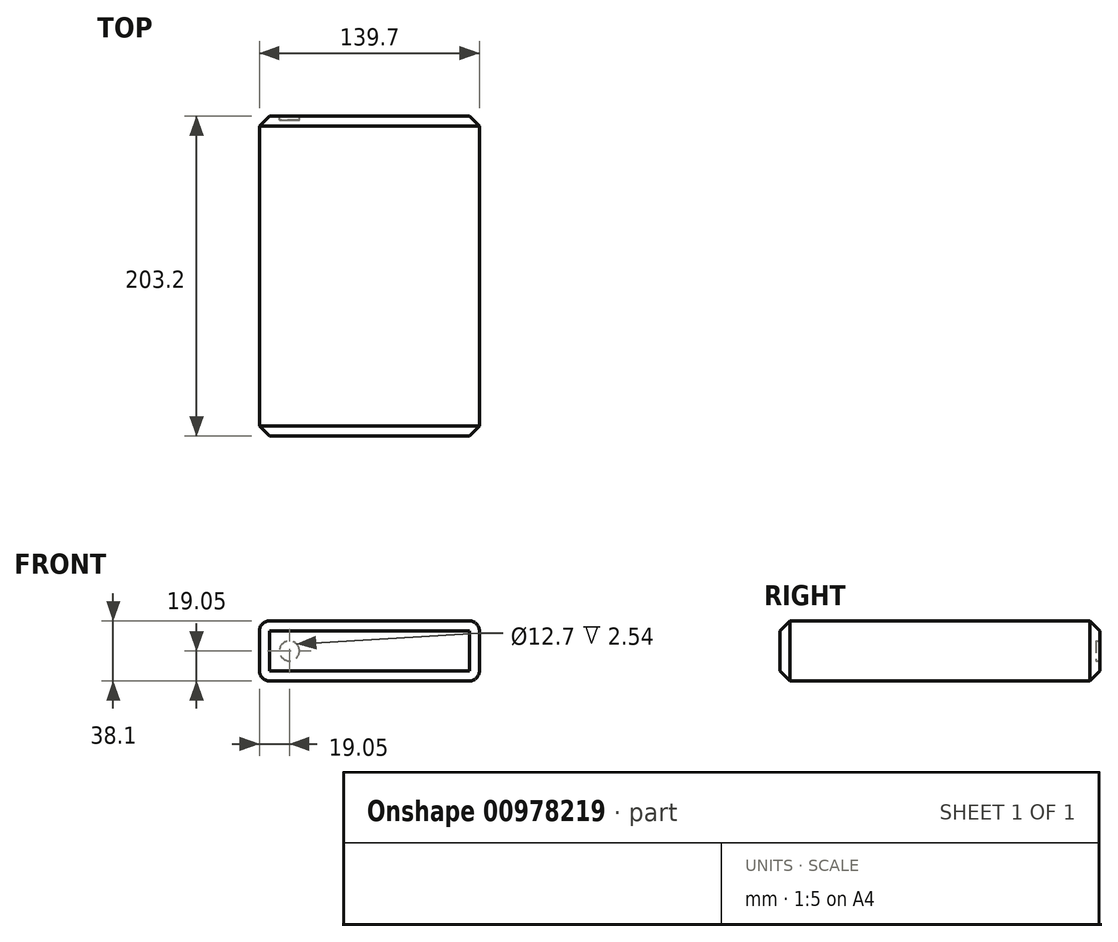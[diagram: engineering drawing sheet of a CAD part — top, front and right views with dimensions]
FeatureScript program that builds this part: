
annotation { "Feature Type Name" : "Feature", "Feature Type Description" : "" }
export const myFeature = defineFeature(function(context is Context, id is Id, definition is map)
    precondition{}
    {
        {
            var Q0;
            Q0=qCreatedBy(makeId("Front.planeOp"),FACE);
            var sketch = newSketch(context, id + "F0", { "sketchPlane" : qUnion([Q0])});
            skLineSegment(sketch, "E0.bottom", {"start": v(-69.85, 19.05) * mm, "end": v(69.85, 19.05) * mm});
            skLineSegment(sketch, "E0.top", {"start": v(-69.85, -19.05) * mm, "end": v(69.85, -19.05) * mm});
            skLineSegment(sketch, "E0.left", {"start": v(-69.85, 19.05) * mm, "end": v(-69.85, -19.05) * mm});
            skLineSegment(sketch, "E0.right", {"start": v(69.85, 19.05) * mm, "end": v(69.85, -19.05) * mm});
            skLineSegment(sketch, "E1", {"start": v(0, 0) * mm, "end": v(0, 19.05) * mm, "construction": true});
            skLineSegment(sketch, "E2", {"start": v(0, 0) * mm, "end": v(69.85, 0) * mm, "construction": true});
            skSolve(sketch);
        }
        {
            var Q0;
            Q0=makeQuery(id+"F0.imprint","IMPRINT",FACE,{"disambiguationData":[TD([[makeQuery(id+"F0.imprint","IMPRINT",EDGE,{"derivedFrom":sQuery(id+"F0.wireOp",EDGE,"E0.bottom")}),-1.0]])]});
            extrude(context, id + "F1", {"entities" : qUnion([Q0]), "depth" : 203.2 * mm, "offsetDistance" : 25.4 * mm});
        }
        {
            var Q0;
            Q0=makeQuery(id+"F1.opExtrude","SWEPT_EDGE",EDGE,{"disambiguationData":[OSD([sQuery(id+"F0.wireOp",EDGE,"E0.bottom"),sQuery(id+"F0.wireOp",EDGE,"E0.left")])]});
            var Q1;
            Q1=makeQuery(id+"F1.opExtrude","SWEPT_EDGE",EDGE,{"disambiguationData":[OSD([sQuery(id+"F0.wireOp",EDGE,"E0.top"),sQuery(id+"F0.wireOp",EDGE,"E0.left")])]});
            var Q2;
            Q2=makeQuery(id+"F1.opExtrude","SWEPT_EDGE",EDGE,{"disambiguationData":[OSD([sQuery(id+"F0.wireOp",EDGE,"E0.bottom"),sQuery(id+"F0.wireOp",EDGE,"E0.right")])]});
            var Q3;
            Q3=makeQuery(id+"F1.opExtrude","SWEPT_EDGE",EDGE,{"disambiguationData":[OSD([sQuery(id+"F0.wireOp",EDGE,"E0.top"),sQuery(id+"F0.wireOp",EDGE,"E0.right")])]});
            fillet(context, id + "F2", {"entities" : qUnion([Q0, Q1, Q2, Q3]), "radius" : 6.35 * mm, "tangentPropagation" : true, "allowEdgeOverflow" : false});
        }
        {
            var Q0;
            Q0=makeQuery(id+"F1.opExtrude","CAP_EDGE",EDGE,{"disambiguationData":[OSD([sQuery(id+"F0.wireOp",EDGE,"E0.bottom")])],"isStart":false});
            chamfer(context, id + "F3", {"entities" : qUnion([Q0]), "width" : 6.35 * mm, "tangentPropagation" : true});
        }
        {
            var Q0;
            Q0=makeQuery(id+"F1.opExtrude","CAP_EDGE",EDGE,{"disambiguationData":[OSD([sQuery(id+"F0.wireOp",EDGE,"E0.bottom")])],"isStart":true});
            chamfer(context, id + "F4", {"entities" : qUnion([Q0]), "width" : 6.35 * mm, "tangentPropagation" : true});
        }
        {
            var Q0;
            Q0=makeQuery(id+"F1.opExtrude","CAP_FACE",FACE,{"disambiguationData":[OSD([sQuery(id+"F0.wireOp",EDGE,"E0.bottom"),sQuery(id+"F0.wireOp",EDGE,"E0.top"),sQuery(id+"F0.wireOp",EDGE,"E0.left"),sQuery(id+"F0.wireOp",EDGE,"E0.right")])],"isStart":true});
            var sketch = newSketch(context, id + "F5", { "sketchPlane" : qUnion([Q0])});
            skCircle(sketch, "E3", {"center": v(50.8, 0) * mm, "radius": 6.35 * mm});
            skSolve(sketch);
        }
        {
            var Q0;
            Q0=makeQuery(id+"F5.imprint","IMPRINT",FACE,{"disambiguationData":[TD([[makeQuery(id+"F5.imprint","IMPRINT",EDGE,{"derivedFrom":sQuery(id+"F5.wireOp",EDGE,"E3")}),1.0]])]});
            extrude(context, id + "F6", {"entities" : qUnion([Q0]), "operationType" : NewBodyOperationType.REMOVE, "oppositeDirection" : true, "depth" : 2.54 * mm, "offsetDistance" : 25.4 * mm});
        }
    });
